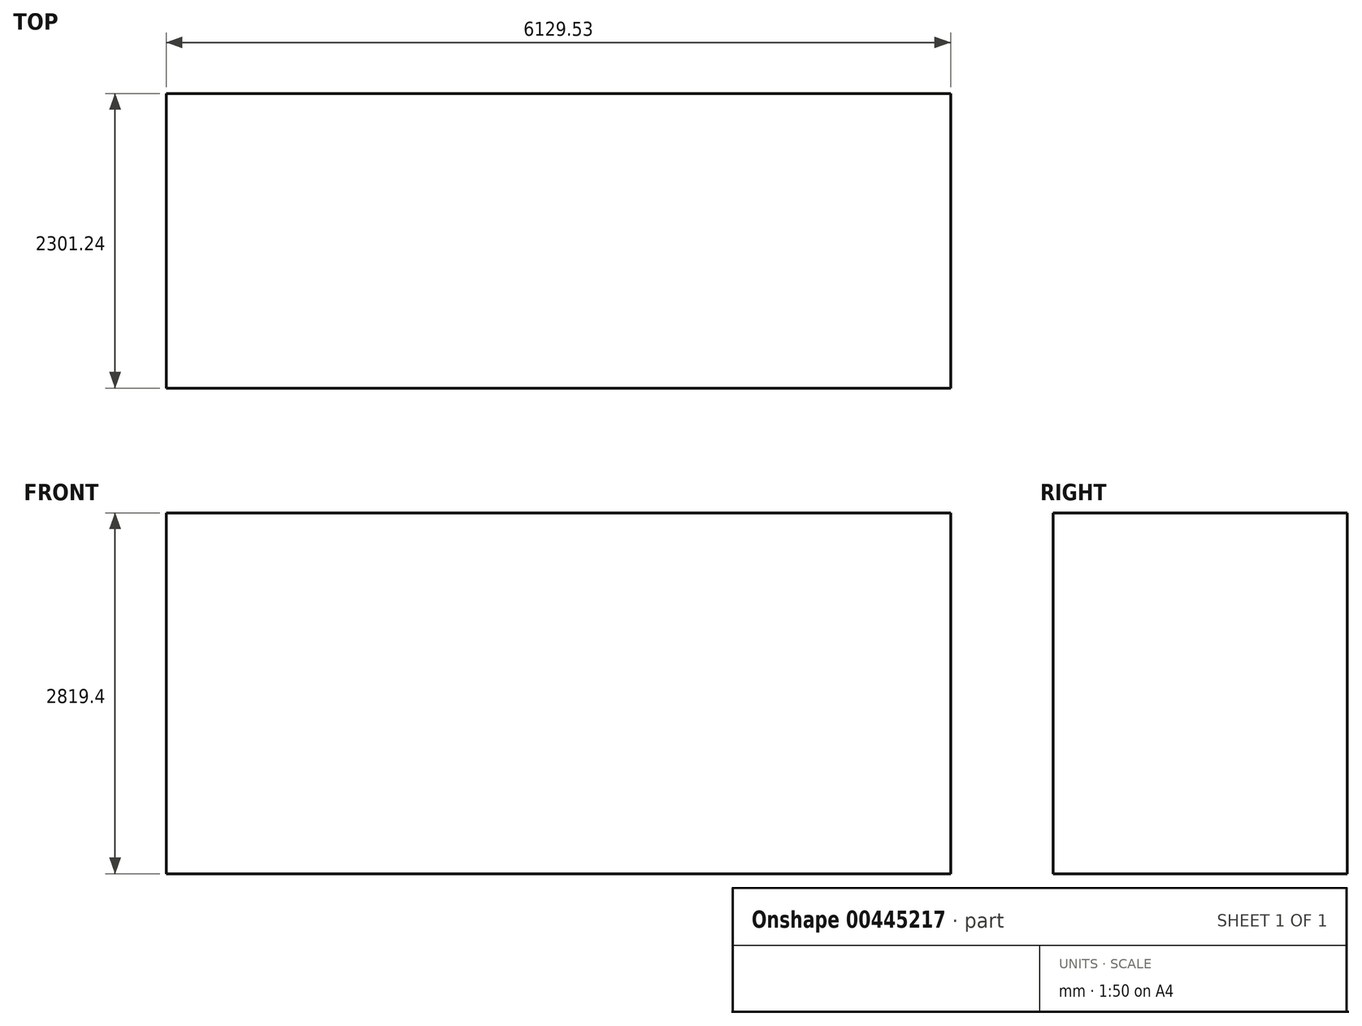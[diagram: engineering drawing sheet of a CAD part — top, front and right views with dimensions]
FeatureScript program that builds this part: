
annotation { "Feature Type Name" : "Feature", "Feature Type Description" : "" }
export const myFeature = defineFeature(function(context is Context, id is Id, definition is map)
    precondition{}
    {
        {
            var Q0;
            Q0=qCreatedBy(makeId("Front.planeOp"),FACE);
            var sketch = newSketch(context, id + "F0", { "sketchPlane" : qUnion([Q0])});
            skLineSegment(sketch, "E0.bottom", {"start": v(-3068.02, 622.58) * mm, "end": v(3061.51, 622.58) * mm});
            skLineSegment(sketch, "E0.top", {"start": v(-3068.02, -2196.82) * mm, "end": v(3061.51, -2196.82) * mm});
            skLineSegment(sketch, "E0.left", {"start": v(-3068.02, 622.58) * mm, "end": v(-3068.02, -2196.82) * mm});
            skLineSegment(sketch, "E0.right", {"start": v(3061.51, 622.58) * mm, "end": v(3061.51, -2196.82) * mm});
            skSolve(sketch);
        }
        {
            var Q0;
            Q0=makeQuery(id+"F0.imprint","IMPRINT",FACE,{"disambiguationData":[TD([[makeQuery(id+"F0.imprint","IMPRINT",EDGE,{"derivedFrom":sQuery(id+"F0.wireOp",EDGE,"E0.bottom")}),-1.0]])]});
            extrude(context, id + "F1", {"entities" : qUnion([Q0]), "depth" : 2301.24 * mm});
        }
    });
